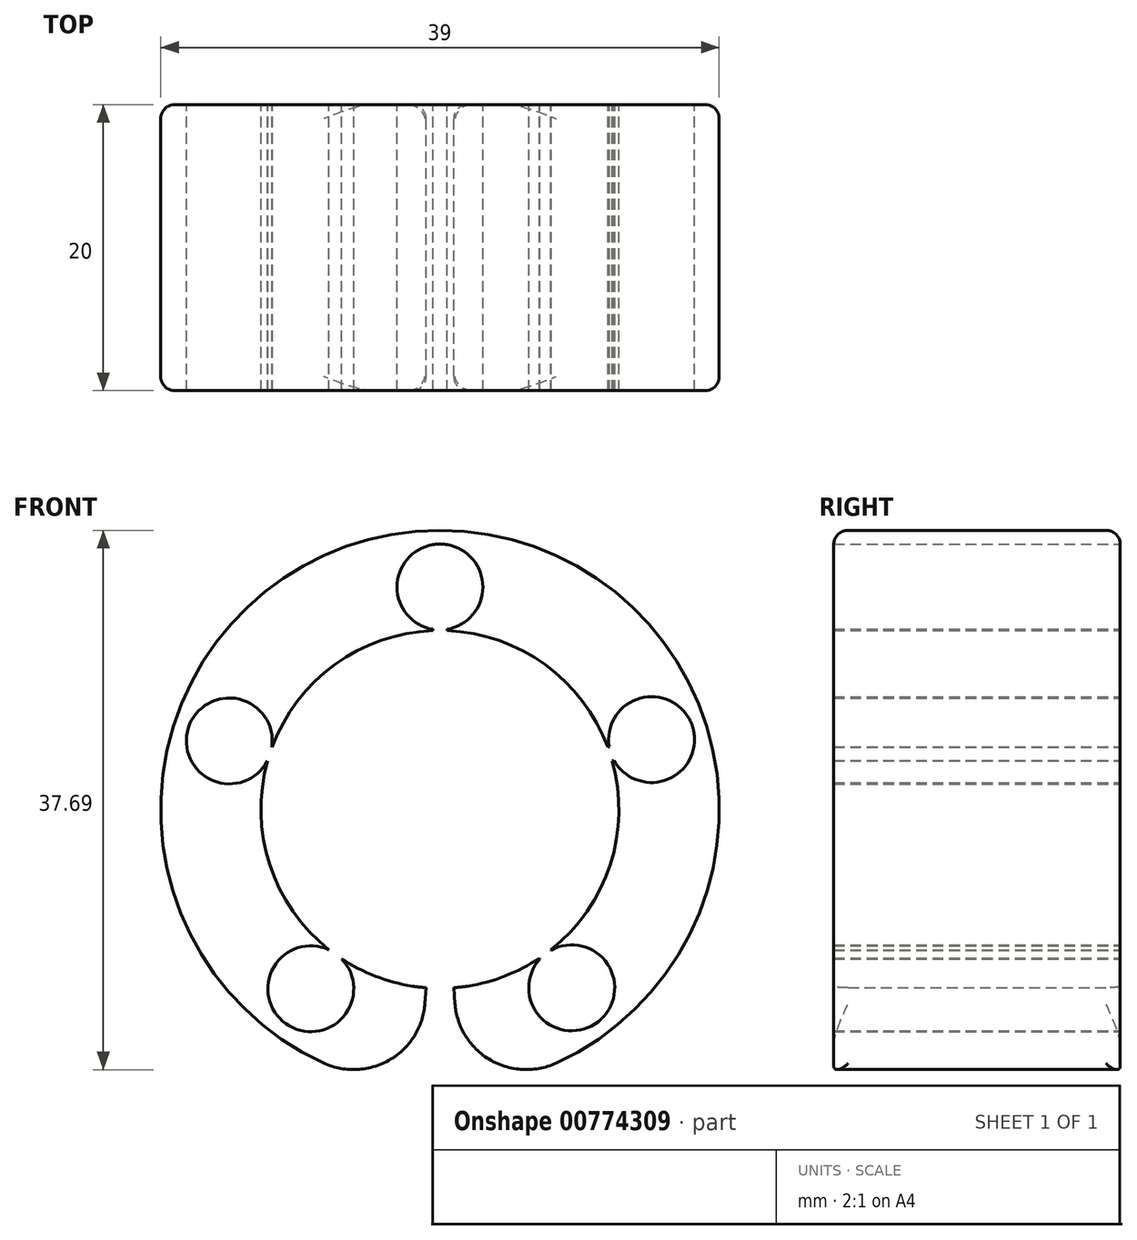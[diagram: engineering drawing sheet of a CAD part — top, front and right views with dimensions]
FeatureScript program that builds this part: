
annotation { "Feature Type Name" : "Feature", "Feature Type Description" : "" }
export const myFeature = defineFeature(function(context is Context, id is Id, definition is map)
    precondition{}
    {
        {
            assignVariable(context, id + "F0", {"name" : "L_CARTUCCIA", "anyValue" : 20});
        }
        {
            var Q0;
            Q0=qCreatedBy(makeId("Front.planeOp"),FACE);
            var sketch = newSketch(context, id + "F1", { "sketchPlane" : qUnion([Q0])});
            skCircle(sketch, "E0", {"center": v(0, 0) * mm, "radius": 12.5 * mm});
            skCircle(sketch, "E1.0", {"center": v(0, 0) * mm, "radius": 19.5 * mm});
            skCircle(sketch, "E2", {"center": v(0, 15.54) * mm, "radius": 3 * mm});
            skCircle(sketch, "E3.1.0", {"center": v(-14.7, 4.78) * mm, "radius": 3 * mm});
            skCircle(sketch, "E3.2.0", {"center": v(-9.02, -12.53) * mm, "radius": 3 * mm});
            skCircle(sketch, "E3.3.0", {"center": v(9.2, -12.47) * mm, "radius": 3 * mm});
            skCircle(sketch, "E3.4.0", {"center": v(14.78, 4.88) * mm, "radius": 3 * mm});
            skPoint(sketch, "E3.center", {"position": v(0.05, 0.04) * mm});
            skLineSegment(sketch, "E4", {"start": v(0, 0) * mm, "end": v(-1.5, -19.44) * mm});
            skLineSegment(sketch, "E5.MirrorCS", {"start": v(0, 0) * mm, "end": v(1.5, -19.44) * mm});
            skCircle(sketch, "E6", {"center": v(0, 0) * mm, "radius": 15.54 * mm, "construction": true});
            skLineSegment(sketch, "E7", {"start": v(-0.5, 15.53) * mm, "end": v(-0.5, 10.07) * mm});
            skLineSegment(sketch, "E8.MirrorCS", {"start": v(0.5, 15.53) * mm, "end": v(0.5, 10.07) * mm});
            skLineSegment(sketch, "E9.1.0", {"start": v(-14.92, 4.32) * mm, "end": v(-9.73, 2.64) * mm});
            skLineSegment(sketch, "E9.1.1", {"start": v(-14.62, 5.27) * mm, "end": v(-9.42, 3.59) * mm});
            skLineSegment(sketch, "E9.2.0", {"start": v(-8.72, -12.86) * mm, "end": v(-5.52, -8.44) * mm});
            skLineSegment(sketch, "E9.2.1", {"start": v(-9.53, -12.27) * mm, "end": v(-6.32, -7.85) * mm});
            skLineSegment(sketch, "E9.3.0", {"start": v(9.53, -12.27) * mm, "end": v(6.32, -7.85) * mm});
            skLineSegment(sketch, "E9.3.1", {"start": v(8.72, -12.86) * mm, "end": v(5.52, -8.44) * mm});
            skLineSegment(sketch, "E9.4.0", {"start": v(14.62, 5.27) * mm, "end": v(9.42, 3.59) * mm});
            skLineSegment(sketch, "E9.4.1", {"start": v(14.92, 4.32) * mm, "end": v(9.73, 2.64) * mm});
            skSolve(sketch);
        }
        {
            var Q0;
            {var subQ1=sQuery(id+"F1.wireOp",EDGE,"E0");var subQ24=sQuery(id+"F1.wireOp",EDGE,"E9.4.0");var subQ38=makeQuery(id+"F1.imprint","INTERSECT",VERTEX,{"derivedFrom":[subQ1,subQ24]});Q0=makeQuery(id+"F1.imprint","IMPRINT",FACE,{"disambiguationData":[TD([[makeQuery(id+"F1.imprint","IMPRINT",EDGE,{"disambiguationData":[TD([[subQ38,-1.0]])],"derivedFrom":subQ1}),-1.0]])]});}
            extrude(context, id + "F2", {"entities" : qUnion([Q0]), "depth" : (getVariable(context, 'L_CARTUCCIA')) * mm, "offsetDistance" : 25 * mm});
        }
        {
            var Q0;
            Q0=makeQuery(id+"F2.opExtrude","CAP_EDGE",EDGE,{"disambiguationData":[OSD([sQuery(id+"F1.wireOp",EDGE,"E1.0")])],"isStart":true});
            var Q1;
            Q1=makeQuery(id+"F2.opExtrude","CAP_EDGE",EDGE,{"disambiguationData":[OSD([sQuery(id+"F1.wireOp",EDGE,"E1.0")])],"isStart":false});
            var Q2;
            Q2=makeQuery(id+"F2.opExtrude","CAP_EDGE",EDGE,{"disambiguationData":[OSD([sQuery(id+"F1.wireOp",EDGE,"E4")])],"isStart":true});
            var Q3;
            Q3=makeQuery(id+"F2.opExtrude","CAP_EDGE",EDGE,{"disambiguationData":[OSD([sQuery(id+"F1.wireOp",EDGE,"E5.MirrorCS")])],"isStart":true});
            var Q4;
            Q4=makeQuery(id+"F2.opExtrude","CAP_EDGE",EDGE,{"disambiguationData":[OSD([sQuery(id+"F1.wireOp",EDGE,"E5.MirrorCS")])],"isStart":false});
            var Q5;
            Q5=makeQuery(id+"F2.opExtrude","CAP_EDGE",EDGE,{"disambiguationData":[OSD([sQuery(id+"F1.wireOp",EDGE,"E4")])],"isStart":false});
            fillet(context, id + "F3", {"entities" : qUnion([Q0, Q1, Q2, Q3, Q4, Q5]), "radius" : 1 * mm, "tangentPropagation" : true, "allowEdgeOverflow" : false});
        }
        {
            var Q0;
            Q0=makeQuery(id+"F2.opExtrude","SWEPT_EDGE",EDGE,{"disambiguationData":[OSD([sQuery(id+"F1.wireOp",EDGE,"E1.0"),sQuery(id+"F1.wireOp",EDGE,"E5.MirrorCS")])]});
            var Q1;
            Q1=makeQuery(id+"F2.opExtrude","SWEPT_EDGE",EDGE,{"disambiguationData":[OSD([sQuery(id+"F1.wireOp",EDGE,"E1.0"),sQuery(id+"F1.wireOp",EDGE,"E4")])]});
            fillet(context, id + "F4", {"entities" : qUnion([Q0, Q1]), "radius" : 5 * mm, "allowEdgeOverflow" : false});
        }
    });
